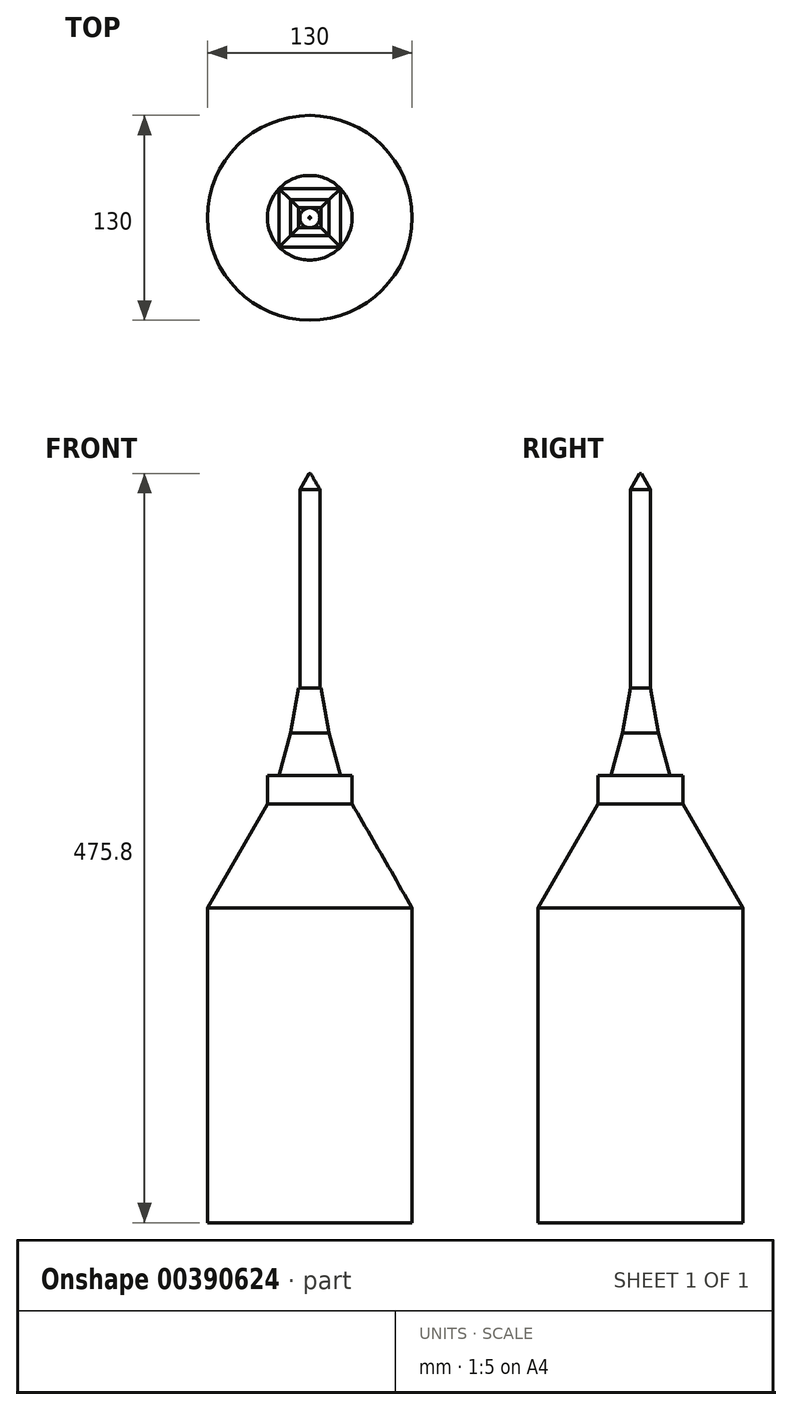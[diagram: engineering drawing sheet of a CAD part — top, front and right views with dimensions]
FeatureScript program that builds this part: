
annotation { "Feature Type Name" : "Feature", "Feature Type Description" : "" }
export const myFeature = defineFeature(function(context is Context, id is Id, definition is map)
    precondition{}
    {
        {
            var Q0;
            Q0=qCreatedBy(makeId("Top.planeOp"),FACE);
            var sketch = newSketch(context, id + "F0", { "sketchPlane" : qUnion([Q0])});
            skCircle(sketch, "E0", {"center": v(0, 0) * mm, "radius": 65 * mm});
            skSolve(sketch);
        }
        {
            var Q0;
            Q0=makeQuery(id+"F0.imprint","IMPRINT",FACE,{"disambiguationData":[TD([[makeQuery(id+"F0.imprint","IMPRINT",EDGE,{"derivedFrom":sQuery(id+"F0.wireOp",EDGE,"E0")}),1.0]])]});
            extrude(context, id + "F1", {"entities" : qUnion([Q0]), "depth" : 200 * mm});
        }
        {
            var Q0;
            Q0=makeQuery(id+"F1.opExtrude","CAP_FACE",FACE,{"disambiguationData":[OSD([sQuery(id+"F0.wireOp",EDGE,"E0")])],"isStart":false});
            var sketch = newSketch(context, id + "F2", { "sketchPlane" : qUnion([Q0])});
            skSolve(sketch);
        }
        {
            var Q0;
            Q0=makeQuery(id+"F2.imprint","IMPRINT",FACE,{"disambiguationData":[TD([[makeQuery(id+"F2.imprint","IMPRINT",EDGE,{"derivedFrom":makeQuery(id+"F1.opExtrude","CAP_EDGE",EDGE,{"disambiguationData":[OSD([sQuery(id+"F0.wireOp",EDGE,"E0")])],"isStart":false})}),1.0]])]});
            extrude(context, id + "F3", {"entities" : qUnion([Q0]), "operationType" : NewBodyOperationType.ADD, "depth" : 66 * mm, "hasDraft" : true, "draftAngle" : 30 * degree, "draftPullDirection" : true});
        }
        {
            var Q0;
            Q0=makeQuery(id+"F3.opExtrude","CAP_FACE",FACE,{"disambiguationData":[OSD([sQuery(id+"F0.wireOp",EDGE,"E0")])],"isStart":false});
            var sketch = newSketch(context, id + "F4", { "sketchPlane" : qUnion([Q0])});
            skSolve(sketch);
        }
        {
            var Q0;
            Q0=makeQuery(id+"F4.imprint","IMPRINT",FACE,{"disambiguationData":[TD([[makeQuery(id+"F4.imprint","IMPRINT",EDGE,{"derivedFrom":makeQuery(id+"F3.opExtrude","CAP_EDGE",EDGE,{"disambiguationData":[OSD([sQuery(id+"F0.wireOp",EDGE,"E0")])],"isStart":false})}),1.0]])]});
            extrude(context, id + "F5", {"entities" : qUnion([Q0]), "operationType" : NewBodyOperationType.ADD, "depth" : 18 * mm});
        }
        {
            var Q0;
            Q0=makeQuery(id+"F5.opExtrude","CAP_FACE",FACE,{"disambiguationData":[OSD([sQuery(id+"F0.wireOp",EDGE,"E0")])],"isStart":false});
            var sketch = newSketch(context, id + "F6", { "sketchPlane" : qUnion([Q0])});
            skLineSegment(sketch, "E1.bottom", {"start": v(-19.4, 18.62) * mm, "end": v(19.4, 18.62) * mm});
            skLineSegment(sketch, "E1.top", {"start": v(-19.4, -18.62) * mm, "end": v(19.4, -18.62) * mm});
            skLineSegment(sketch, "E1.left", {"start": v(-19.4, 18.62) * mm, "end": v(-19.4, -18.62) * mm});
            skLineSegment(sketch, "E1.right", {"start": v(19.4, 18.62) * mm, "end": v(19.4, -18.62) * mm});
            skSolve(sketch);
        }
        {
            var Q0;
            Q0=makeQuery(id+"F6.imprint","IMPRINT",FACE,{"disambiguationData":[TD([[makeQuery(id+"F6.imprint","IMPRINT",EDGE,{"derivedFrom":sQuery(id+"F6.wireOp",EDGE,"E1.bottom")}),-1.0]])]});
            extrude(context, id + "F7", {"entities" : qUnion([Q0]), "operationType" : NewBodyOperationType.ADD, "depth" : 26.9 * mm, "hasDraft" : true, "draftAngle" : 15 * degree, "draftPullDirection" : true});
        }
        {
            var Q0;
            Q0=makeQuery(id+"F7.opExtrude","CAP_FACE",FACE,{"disambiguationData":[OSD([sQuery(id+"F6.wireOp",EDGE,"E1.bottom"),sQuery(id+"F6.wireOp",EDGE,"E1.top"),sQuery(id+"F6.wireOp",EDGE,"E1.left"),sQuery(id+"F6.wireOp",EDGE,"E1.right")])],"isStart":false});
            extrude(context, id + "F8", {"entities" : qUnion([Q0]), "operationType" : NewBodyOperationType.ADD, "depth" : 28.7 * mm, "hasDraft" : true, "draftAngle" : 10 * degree, "draftPullDirection" : true});
        }
        {
            var Q0;
            Q0=makeQuery(id+"F8.opExtrude","CAP_FACE",FACE,{"disambiguationData":[OSD([sQuery(id+"F6.wireOp",EDGE,"E1.bottom"),sQuery(id+"F6.wireOp",EDGE,"E1.top"),sQuery(id+"F6.wireOp",EDGE,"E1.left"),sQuery(id+"F6.wireOp",EDGE,"E1.right")])],"isStart":false});
            var sketch = newSketch(context, id + "F9", { "sketchPlane" : qUnion([Q0])});
            skCircle(sketch, "E2", {"center": v(0, 0) * mm, "radius": 6.35 * mm});
            skSolve(sketch);
        }
        {
            var Q0;
            {var subQ0=sQuery(id+"F9.wireOp",EDGE,"E2");var subQ1=makeQuery(id+"F9.imprint","INTERSECT",VERTEX,{"derivedFrom":[makeQuery(id+"F8.opExtrude","CAP_EDGE",EDGE,{"disambiguationData":[OSD([sQuery(id+"F6.wireOp",EDGE,"E1.bottom")])],"isStart":false}),subQ0]});Q0=makeQuery(id+"F9.imprint","IMPRINT",FACE,{"disambiguationData":[TD([[makeQuery(id+"F9.imprint","IMPRINT",EDGE,{"disambiguationData":[TD([[subQ1,-1.0]])],"derivedFrom":subQ0}),1.0]])]});}
            extrude(context, id + "F10", {"entities" : qUnion([Q0]), "operationType" : NewBodyOperationType.ADD, "depth" : 126.2 * mm});
        }
        {
            var Q0;
            Q0=makeQuery(id+"F10.opExtrude","CAP_FACE",FACE,{"disambiguationData":[OSD([sQuery(id+"F9.wireOp",EDGE,"E2")])],"isStart":false});
            var sketch = newSketch(context, id + "F11", { "sketchPlane" : qUnion([Q0])});
            skSolve(sketch);
        }
        {
            var Q0;
            Q0 = qSketchRegion(id + "F11", true);
            var Q1;
            Q1=makeQuery(id+"F11.imprint","IMPRINT",FACE,{"disambiguationData":[TD([[makeQuery(id+"F11.imprint","IMPRINT",EDGE,{"derivedFrom":makeQuery(id+"F10.opExtrude","CAP_EDGE",EDGE,{"disambiguationData":[OSD([sQuery(id+"F9.wireOp",EDGE,"E2")])],"isStart":false})}),1.0]])]});
            var Q2;
            Q2=makeQuery(id+"F10.opExtrude","CAP_FACE",FACE,{"disambiguationData":[OSD([sQuery(id+"F9.wireOp",EDGE,"E2")])],"isStart":false});
            extrude(context, id + "F12", {"entities" : qUnion([Q0, Q1, Q2]), "operationType" : NewBodyOperationType.ADD, "depth" : 10 * mm, "hasDraft" : true, "draftAngle" : 30 * degree, "draftPullDirection" : true});
        }
    });
